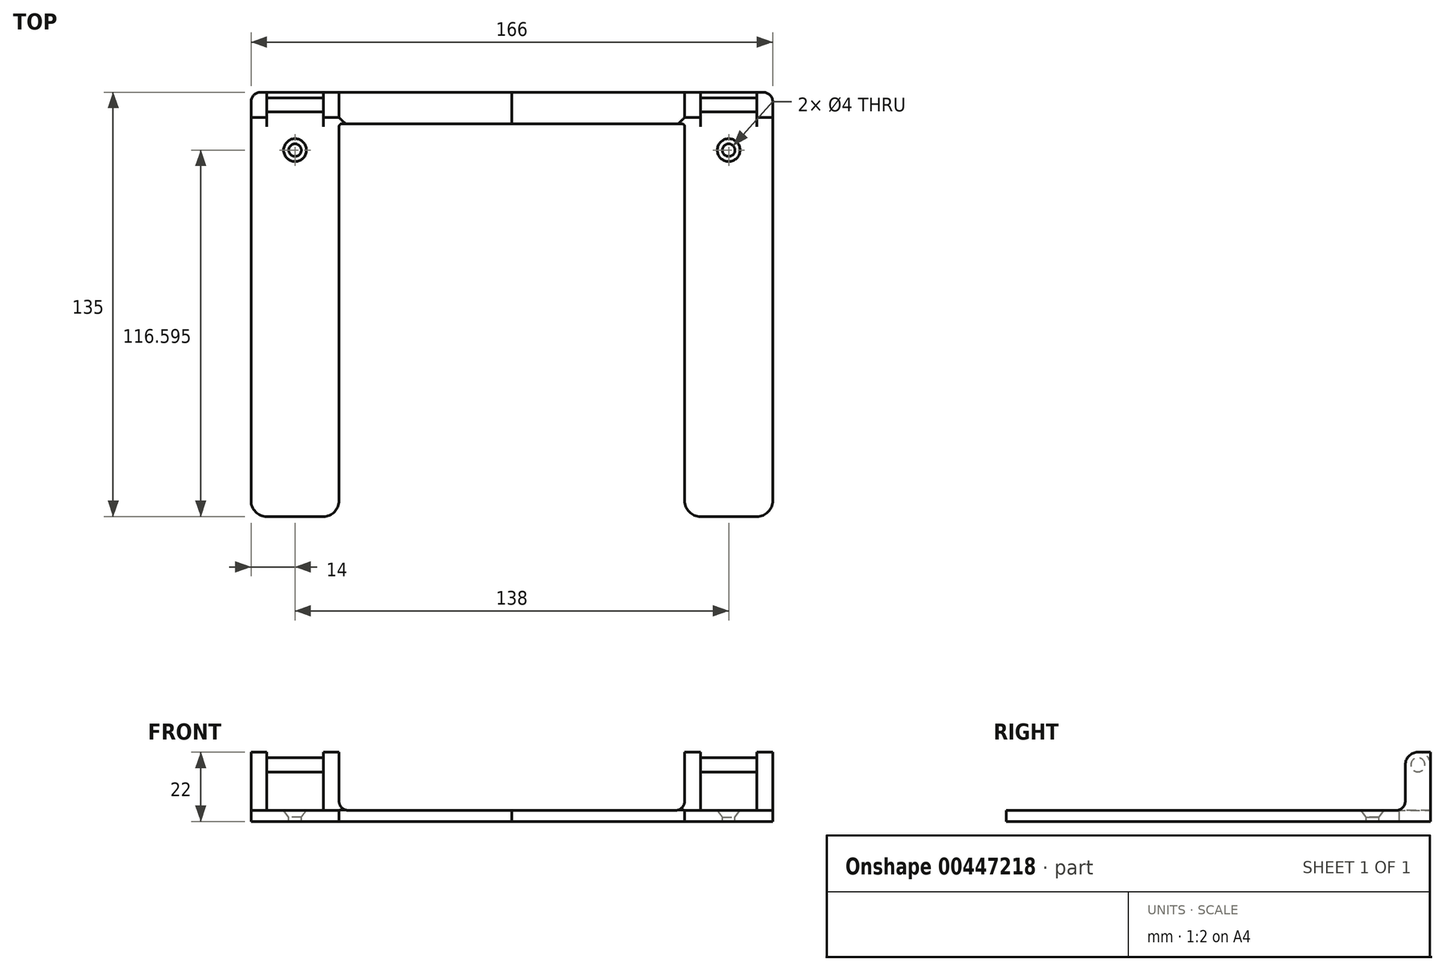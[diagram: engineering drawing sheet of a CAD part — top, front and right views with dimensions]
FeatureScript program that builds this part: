
annotation { "Feature Type Name" : "Feature", "Feature Type Description" : "" }
export const myFeature = defineFeature(function(context is Context, id is Id, definition is map)
    precondition{}
    {
        {
            var Q0;
            Q0=qCreatedBy(makeId("Top.planeOp"),FACE);
            var sketch = newSketch(context, id + "F0", { "sketchPlane" : qUnion([Q0])});
            skLineSegment(sketch, "E0.bottom", {"start": v(-83, 0) * mm, "end": v(-55, 0) * mm});
            skLineSegment(sketch, "E0.top", {"start": v(-83, 135) * mm, "end": v(0, 135) * mm});
            skLineSegment(sketch, "E0.left", {"start": v(-83, 0) * mm, "end": v(-83, 135) * mm});
            skLineSegment(sketch, "E1.top", {"start": v(-55, 125) * mm, "end": v(0, 125) * mm});
            skLineSegment(sketch, "E1.left", {"start": v(-55, 0) * mm, "end": v(-55, 125) * mm});
            skLineSegment(sketch, "E2", {"start": v(0, 135) * mm, "end": v(0, 125) * mm});
            skSolve(sketch);
        }
        {
            var Q0;
            Q0=qCreatedBy(makeId("Top.planeOp"),FACE);
            var sketch = newSketch(context, id + "F1", { "sketchPlane" : qUnion([Q0])});
            skLineSegment(sketch, "E3", {"start": v(-65.03, 100.86) * mm, "end": v(-64.7, 100.94) * mm});
            skLineSegment(sketch, "E4", {"start": v(-64.7, 100.94) * mm, "end": v(-62.94, 101.35) * mm});
            skLineSegment(sketch, "E5", {"start": v(-62.94, 101.35) * mm, "end": v(-61.22, 101.8) * mm});
            skLineSegment(sketch, "E6", {"start": v(-61.22, 101.8) * mm, "end": v(-60.9, 101.9) * mm});
            skLineSegment(sketch, "E7", {"start": v(-60.9, 101.9) * mm, "end": v(-60.65, 101.57) * mm});
            skLineSegment(sketch, "E8", {"start": v(-60.65, 101.57) * mm, "end": v(-60.06, 100.49) * mm});
            skLineSegment(sketch, "E9", {"start": v(-60.06, 100.49) * mm, "end": v(-59.39, 98.73) * mm});
            skLineSegment(sketch, "E10", {"start": v(-59.39, 98.73) * mm, "end": v(-58.9, 96.76) * mm});
            skLineSegment(sketch, "E11", {"start": v(-58.9, 96.76) * mm, "end": v(-58.67, 95.22) * mm});
            skLineSegment(sketch, "E12", {"start": v(-58.67, 95.22) * mm, "end": v(-58.64, 94.7) * mm});
            skLineSegment(sketch, "E13", {"start": v(-58.64, 94.7) * mm, "end": v(-58.62, 94.42) * mm});
            skLineSegment(sketch, "E14", {"start": v(-58.62, 94.42) * mm, "end": v(-58.62, 93.57) * mm});
            skLineSegment(sketch, "E15", {"start": v(-58.62, 93.57) * mm, "end": v(-58.71, 92.38) * mm});
            skLineSegment(sketch, "E16", {"start": v(-58.71, 92.38) * mm, "end": v(-58.94, 91.24) * mm});
            skLineSegment(sketch, "E17", {"start": v(-58.94, 91.24) * mm, "end": v(-59.32, 90.2) * mm});
            skLineSegment(sketch, "E18", {"start": v(-59.32, 90.2) * mm, "end": v(-59.87, 89.36) * mm});
            skLineSegment(sketch, "E19", {"start": v(-59.87, 89.36) * mm, "end": v(-60.6, 88.77) * mm});
            skLineSegment(sketch, "E20", {"start": v(-60.6, 88.77) * mm, "end": v(-61.53, 88.53) * mm});
            skLineSegment(sketch, "E21", {"start": v(-61.53, 88.53) * mm, "end": v(-62.4, 88.62) * mm});
            skLineSegment(sketch, "E22", {"start": v(-62.4, 88.62) * mm, "end": v(-62.67, 88.7) * mm});
            skLineSegment(sketch, "E23", {"start": v(-62.67, 88.7) * mm, "end": v(-63.05, 88.83) * mm});
            skLineSegment(sketch, "E24", {"start": v(-63.05, 88.83) * mm, "end": v(-64, 89.74) * mm});
            skLineSegment(sketch, "E25", {"start": v(-64, 89.74) * mm, "end": v(-65.04, 91.61) * mm});
            skLineSegment(sketch, "E26", {"start": v(-65.04, 91.61) * mm, "end": v(-65.65, 93.9) * mm});
            skLineSegment(sketch, "E27", {"start": v(-65.65, 93.9) * mm, "end": v(-65.79, 95.62) * mm});
            skLineSegment(sketch, "E28", {"start": v(-65.79, 95.62) * mm, "end": v(-65.72, 96.18) * mm});
            skLineSegment(sketch, "E29", {"start": v(-65.72, 96.18) * mm, "end": v(-65.69, 96.48) * mm});
            skLineSegment(sketch, "E30", {"start": v(-65.69, 96.48) * mm, "end": v(-65.51, 97.34) * mm});
            skLineSegment(sketch, "E31", {"start": v(-65.51, 97.34) * mm, "end": v(-65.24, 98.48) * mm});
            skLineSegment(sketch, "E32", {"start": v(-65.24, 98.48) * mm, "end": v(-65.03, 99.63) * mm});
            skLineSegment(sketch, "E33", {"start": v(-65.03, 99.63) * mm, "end": v(-65, 100.56) * mm});
            skLineSegment(sketch, "E34", {"start": v(-65, 100.56) * mm, "end": v(-65.03, 100.86) * mm});
            skLineSegment(sketch, "E35", {"start": v(-61.35, 103.49) * mm, "end": v(-61.66, 103.4) * mm});
            skLineSegment(sketch, "E36", {"start": v(-61.66, 103.4) * mm, "end": v(-63.42, 102.9) * mm});
            skLineSegment(sketch, "E37", {"start": v(-63.42, 102.9) * mm, "end": v(-65.16, 102.4) * mm});
            skLineSegment(sketch, "E38", {"start": v(-65.16, 102.4) * mm, "end": v(-65.46, 102.29) * mm});
            skLineSegment(sketch, "E39", {"start": v(-65.46, 102.29) * mm, "end": v(-65.6, 102.47) * mm});
            skLineSegment(sketch, "E40", {"start": v(-65.6, 102.47) * mm, "end": v(-65.92, 103.1) * mm});
            skLineSegment(sketch, "E41", {"start": v(-65.92, 103.1) * mm, "end": v(-66.24, 104.13) * mm});
            skLineSegment(sketch, "E42", {"start": v(-66.24, 104.13) * mm, "end": v(-66.38, 105.27) * mm});
            skLineSegment(sketch, "E43", {"start": v(-66.38, 105.27) * mm, "end": v(-66.32, 106.4) * mm});
            skLineSegment(sketch, "E44", {"start": v(-66.32, 106.4) * mm, "end": v(-66.03, 107.39) * mm});
            skLineSegment(sketch, "E45", {"start": v(-66.03, 107.39) * mm, "end": v(-65.5, 108.1) * mm});
            skLineSegment(sketch, "E46", {"start": v(-65.5, 108.1) * mm, "end": v(-64.69, 108.43) * mm});
            skLineSegment(sketch, "E47", {"start": v(-64.69, 108.43) * mm, "end": v(-63.83, 108.35) * mm});
            skLineSegment(sketch, "E48", {"start": v(-63.83, 108.35) * mm, "end": v(-63.57, 108.25) * mm});
            skLineSegment(sketch, "E49", {"start": v(-63.57, 108.25) * mm, "end": v(-63.3, 108.15) * mm});
            skLineSegment(sketch, "E50", {"start": v(-63.3, 108.15) * mm, "end": v(-62.62, 107.55) * mm});
            skLineSegment(sketch, "E51", {"start": v(-62.62, 107.55) * mm, "end": v(-61.96, 106.43) * mm});
            skLineSegment(sketch, "E52", {"start": v(-61.96, 106.43) * mm, "end": v(-61.55, 105.02) * mm});
            skLineSegment(sketch, "E53", {"start": v(-61.55, 105.02) * mm, "end": v(-61.38, 103.87) * mm});
            skLineSegment(sketch, "E54", {"start": v(-61.38, 103.87) * mm, "end": v(-61.35, 103.49) * mm});
            skLineSegment(sketch, "E55", {"start": v(-63.75, 67.11) * mm, "end": v(-63.4, 67.18) * mm});
            skLineSegment(sketch, "E56", {"start": v(-63.4, 67.18) * mm, "end": v(-61.65, 67.55) * mm});
            skLineSegment(sketch, "E57", {"start": v(-61.65, 67.55) * mm, "end": v(-59.91, 67.96) * mm});
            skLineSegment(sketch, "E58", {"start": v(-59.91, 67.96) * mm, "end": v(-59.6, 68.04) * mm});
            skLineSegment(sketch, "E59", {"start": v(-59.6, 68.04) * mm, "end": v(-59.35, 67.72) * mm});
            skLineSegment(sketch, "E60", {"start": v(-59.35, 67.72) * mm, "end": v(-58.79, 66.62) * mm});
            skLineSegment(sketch, "E61", {"start": v(-58.79, 66.62) * mm, "end": v(-58.15, 64.85) * mm});
            skLineSegment(sketch, "E62", {"start": v(-58.15, 64.85) * mm, "end": v(-57.71, 62.87) * mm});
            skLineSegment(sketch, "E63", {"start": v(-57.71, 62.87) * mm, "end": v(-57.52, 61.33) * mm});
            skLineSegment(sketch, "E64", {"start": v(-57.52, 61.33) * mm, "end": v(-57.5, 60.81) * mm});
            skLineSegment(sketch, "E65", {"start": v(-57.5, 60.81) * mm, "end": v(-57.48, 60.53) * mm});
            skLineSegment(sketch, "E66", {"start": v(-57.48, 60.53) * mm, "end": v(-57.5, 59.67) * mm});
            skLineSegment(sketch, "E67", {"start": v(-57.5, 59.67) * mm, "end": v(-57.63, 58.49) * mm});
            skLineSegment(sketch, "E68", {"start": v(-57.63, 58.49) * mm, "end": v(-57.88, 57.35) * mm});
            skLineSegment(sketch, "E69", {"start": v(-57.88, 57.35) * mm, "end": v(-58.29, 56.32) * mm});
            skLineSegment(sketch, "E70", {"start": v(-58.29, 56.32) * mm, "end": v(-58.85, 55.49) * mm});
            skLineSegment(sketch, "E71", {"start": v(-58.85, 55.49) * mm, "end": v(-59.6, 54.92) * mm});
            skLineSegment(sketch, "E72", {"start": v(-59.6, 54.92) * mm, "end": v(-60.53, 54.7) * mm});
            skLineSegment(sketch, "E73", {"start": v(-60.53, 54.7) * mm, "end": v(-61.4, 54.81) * mm});
            skLineSegment(sketch, "E74", {"start": v(-61.4, 54.81) * mm, "end": v(-61.67, 54.9) * mm});
            skLineSegment(sketch, "E75", {"start": v(-61.67, 54.9) * mm, "end": v(-62.04, 55.04) * mm});
            skLineSegment(sketch, "E76", {"start": v(-62.04, 55.04) * mm, "end": v(-62.98, 55.97) * mm});
            skLineSegment(sketch, "E77", {"start": v(-62.98, 55.97) * mm, "end": v(-63.97, 57.86) * mm});
            skLineSegment(sketch, "E78", {"start": v(-63.97, 57.86) * mm, "end": v(-64.53, 60.17) * mm});
            skLineSegment(sketch, "E79", {"start": v(-64.53, 60.17) * mm, "end": v(-64.62, 61.9) * mm});
            skLineSegment(sketch, "E80", {"start": v(-64.62, 61.9) * mm, "end": v(-64.54, 62.45) * mm});
            skLineSegment(sketch, "E81", {"start": v(-64.54, 62.45) * mm, "end": v(-64.5, 62.74) * mm});
            skLineSegment(sketch, "E82", {"start": v(-64.5, 62.74) * mm, "end": v(-64.3, 63.6) * mm});
            skLineSegment(sketch, "E83", {"start": v(-64.3, 63.6) * mm, "end": v(-64, 64.73) * mm});
            skLineSegment(sketch, "E84", {"start": v(-64, 64.73) * mm, "end": v(-63.77, 65.88) * mm});
            skLineSegment(sketch, "E85", {"start": v(-63.77, 65.88) * mm, "end": v(-63.72, 66.8) * mm});
            skLineSegment(sketch, "E86", {"start": v(-63.72, 66.8) * mm, "end": v(-63.75, 67.11) * mm});
            skLineSegment(sketch, "E87", {"start": v(-60, 69.65) * mm, "end": v(-60.32, 69.56) * mm});
            skLineSegment(sketch, "E88", {"start": v(-60.32, 69.56) * mm, "end": v(-62.08, 69.11) * mm});
            skLineSegment(sketch, "E89", {"start": v(-62.08, 69.11) * mm, "end": v(-63.83, 68.64) * mm});
            skLineSegment(sketch, "E90", {"start": v(-63.83, 68.64) * mm, "end": v(-64.14, 68.55) * mm});
            skLineSegment(sketch, "E91", {"start": v(-64.14, 68.55) * mm, "end": v(-64.28, 68.73) * mm});
            skLineSegment(sketch, "E92", {"start": v(-64.28, 68.73) * mm, "end": v(-64.59, 69.36) * mm});
            skLineSegment(sketch, "E93", {"start": v(-64.59, 69.36) * mm, "end": v(-64.88, 70.4) * mm});
            skLineSegment(sketch, "E94", {"start": v(-64.88, 70.4) * mm, "end": v(-65, 71.55) * mm});
            skLineSegment(sketch, "E95", {"start": v(-65, 71.55) * mm, "end": v(-64.9, 72.68) * mm});
            skLineSegment(sketch, "E96", {"start": v(-64.9, 72.68) * mm, "end": v(-64.6, 73.66) * mm});
            skLineSegment(sketch, "E97", {"start": v(-64.6, 73.66) * mm, "end": v(-64.04, 74.36) * mm});
            skLineSegment(sketch, "E98", {"start": v(-64.04, 74.36) * mm, "end": v(-63.22, 74.67) * mm});
            skLineSegment(sketch, "E99", {"start": v(-63.22, 74.67) * mm, "end": v(-62.37, 74.56) * mm});
            skLineSegment(sketch, "E100", {"start": v(-62.37, 74.56) * mm, "end": v(-62.12, 74.46) * mm});
            skLineSegment(sketch, "E101", {"start": v(-62.12, 74.46) * mm, "end": v(-61.86, 74.35) * mm});
            skLineSegment(sketch, "E102", {"start": v(-61.86, 74.35) * mm, "end": v(-61.18, 73.74) * mm});
            skLineSegment(sketch, "E103", {"start": v(-61.18, 73.74) * mm, "end": v(-60.54, 72.6) * mm});
            skLineSegment(sketch, "E104", {"start": v(-60.54, 72.6) * mm, "end": v(-60.17, 71.19) * mm});
            skLineSegment(sketch, "E105", {"start": v(-60.17, 71.19) * mm, "end": v(-60.02, 70.03) * mm});
            skLineSegment(sketch, "E106", {"start": v(-60.02, 70.03) * mm, "end": v(-60, 69.65) * mm});
            skLineSegment(sketch, "E107", {"start": v(-63.53, 33.44) * mm, "end": v(-63.18, 33.48) * mm});
            skLineSegment(sketch, "E108", {"start": v(-63.18, 33.48) * mm, "end": v(-61.4, 33.74) * mm});
            skLineSegment(sketch, "E109", {"start": v(-61.4, 33.74) * mm, "end": v(-59.64, 34.03) * mm});
            skLineSegment(sketch, "E110", {"start": v(-59.64, 34.03) * mm, "end": v(-59.32, 34.09) * mm});
            skLineSegment(sketch, "E111", {"start": v(-59.32, 34.09) * mm, "end": v(-59.1, 33.74) * mm});
            skLineSegment(sketch, "E112", {"start": v(-59.1, 33.74) * mm, "end": v(-58.62, 32.6) * mm});
            skLineSegment(sketch, "E113", {"start": v(-58.62, 32.6) * mm, "end": v(-58.1, 30.8) * mm});
            skLineSegment(sketch, "E114", {"start": v(-58.1, 30.8) * mm, "end": v(-57.8, 28.79) * mm});
            skLineSegment(sketch, "E115", {"start": v(-57.8, 28.79) * mm, "end": v(-57.72, 27.24) * mm});
            skLineSegment(sketch, "E116", {"start": v(-57.72, 27.24) * mm, "end": v(-57.73, 26.72) * mm});
            skLineSegment(sketch, "E117", {"start": v(-57.73, 26.72) * mm, "end": v(-57.74, 26.44) * mm});
            skLineSegment(sketch, "E118", {"start": v(-57.74, 26.44) * mm, "end": v(-57.82, 25.58) * mm});
            skLineSegment(sketch, "E119", {"start": v(-57.82, 25.58) * mm, "end": v(-58.02, 24.41) * mm});
            skLineSegment(sketch, "E120", {"start": v(-58.02, 24.41) * mm, "end": v(-58.36, 23.3) * mm});
            skLineSegment(sketch, "E121", {"start": v(-58.36, 23.3) * mm, "end": v(-58.83, 22.3) * mm});
            skLineSegment(sketch, "E122", {"start": v(-58.83, 22.3) * mm, "end": v(-59.45, 21.5) * mm});
            skLineSegment(sketch, "E123", {"start": v(-59.45, 21.5) * mm, "end": v(-60.23, 21) * mm});
            skLineSegment(sketch, "E124", {"start": v(-60.23, 21) * mm, "end": v(-61.18, 20.84) * mm});
            skLineSegment(sketch, "E125", {"start": v(-61.18, 20.84) * mm, "end": v(-62.04, 21.01) * mm});
            skLineSegment(sketch, "E126", {"start": v(-62.04, 21.01) * mm, "end": v(-62.3, 21.12) * mm});
            skLineSegment(sketch, "E127", {"start": v(-62.3, 21.12) * mm, "end": v(-62.67, 21.28) * mm});
            skLineSegment(sketch, "E128", {"start": v(-62.67, 21.28) * mm, "end": v(-63.54, 22.27) * mm});
            skLineSegment(sketch, "E129", {"start": v(-63.54, 22.27) * mm, "end": v(-64.4, 24.23) * mm});
            skLineSegment(sketch, "E130", {"start": v(-64.4, 24.23) * mm, "end": v(-64.8, 26.57) * mm});
            skLineSegment(sketch, "E131", {"start": v(-64.8, 26.57) * mm, "end": v(-64.76, 28.3) * mm});
            skLineSegment(sketch, "E132", {"start": v(-64.76, 28.3) * mm, "end": v(-64.65, 28.85) * mm});
            skLineSegment(sketch, "E133", {"start": v(-64.65, 28.85) * mm, "end": v(-64.59, 29.14) * mm});
            skLineSegment(sketch, "E134", {"start": v(-64.59, 29.14) * mm, "end": v(-64.33, 29.99) * mm});
            skLineSegment(sketch, "E135", {"start": v(-64.33, 29.99) * mm, "end": v(-63.95, 31.09) * mm});
            skLineSegment(sketch, "E136", {"start": v(-63.95, 31.09) * mm, "end": v(-63.64, 32.22) * mm});
            skLineSegment(sketch, "E137", {"start": v(-63.64, 32.22) * mm, "end": v(-63.52, 33.14) * mm});
            skLineSegment(sketch, "E138", {"start": v(-63.52, 33.14) * mm, "end": v(-63.53, 33.44) * mm});
            skLineSegment(sketch, "E139", {"start": v(-59.62, 35.71) * mm, "end": v(-59.93, 35.65) * mm});
            skLineSegment(sketch, "E140", {"start": v(-59.93, 35.65) * mm, "end": v(-61.73, 35.32) * mm});
            skLineSegment(sketch, "E141", {"start": v(-61.73, 35.32) * mm, "end": v(-63.5, 34.98) * mm});
            skLineSegment(sketch, "E142", {"start": v(-63.5, 34.98) * mm, "end": v(-63.82, 34.9) * mm});
            skLineSegment(sketch, "E143", {"start": v(-63.82, 34.9) * mm, "end": v(-63.95, 35.1) * mm});
            skLineSegment(sketch, "E144", {"start": v(-63.95, 35.1) * mm, "end": v(-64.2, 35.75) * mm});
            skLineSegment(sketch, "E145", {"start": v(-64.2, 35.75) * mm, "end": v(-64.43, 36.8) * mm});
            skLineSegment(sketch, "E146", {"start": v(-64.43, 36.8) * mm, "end": v(-64.46, 37.96) * mm});
            skLineSegment(sketch, "E147", {"start": v(-64.46, 37.96) * mm, "end": v(-64.3, 39.08) * mm});
            skLineSegment(sketch, "E148", {"start": v(-64.3, 39.08) * mm, "end": v(-63.92, 40.03) * mm});
            skLineSegment(sketch, "E149", {"start": v(-63.92, 40.03) * mm, "end": v(-63.31, 40.7) * mm});
            skLineSegment(sketch, "E150", {"start": v(-63.31, 40.7) * mm, "end": v(-62.48, 40.95) * mm});
            skLineSegment(sketch, "E151", {"start": v(-62.48, 40.95) * mm, "end": v(-61.64, 40.78) * mm});
            skLineSegment(sketch, "E152", {"start": v(-61.64, 40.78) * mm, "end": v(-61.39, 40.66) * mm});
            skLineSegment(sketch, "E153", {"start": v(-61.39, 40.66) * mm, "end": v(-61.13, 40.53) * mm});
            skLineSegment(sketch, "E154", {"start": v(-61.13, 40.53) * mm, "end": v(-60.5, 39.88) * mm});
            skLineSegment(sketch, "E155", {"start": v(-60.5, 39.88) * mm, "end": v(-59.95, 38.7) * mm});
            skLineSegment(sketch, "E156", {"start": v(-59.95, 38.7) * mm, "end": v(-59.67, 37.26) * mm});
            skLineSegment(sketch, "E157", {"start": v(-59.67, 37.26) * mm, "end": v(-59.6, 36.1) * mm});
            skLineSegment(sketch, "E158", {"start": v(-59.6, 36.1) * mm, "end": v(-59.62, 35.71) * mm});
            skLineSegment(sketch, "E159", {"start": v(-73.59, 84.3) * mm, "end": v(-73.93, 84.31) * mm});
            skLineSegment(sketch, "E160", {"start": v(-73.93, 84.31) * mm, "end": v(-75.73, 84.38) * mm});
            skLineSegment(sketch, "E161", {"start": v(-75.73, 84.38) * mm, "end": v(-77.5, 84.5) * mm});
            skLineSegment(sketch, "E162", {"start": v(-77.5, 84.5) * mm, "end": v(-77.84, 84.52) * mm});
            skLineSegment(sketch, "E163", {"start": v(-77.84, 84.52) * mm, "end": v(-78.06, 84.07) * mm});
            skLineSegment(sketch, "E164", {"start": v(-78.06, 84.07) * mm, "end": v(-78.72, 81.12) * mm});
            skLineSegment(sketch, "E165", {"start": v(-78.72, 81.12) * mm, "end": v(-78.76, 77.7) * mm});
            skLineSegment(sketch, "E166", {"start": v(-78.76, 77.7) * mm, "end": v(-78.67, 77.03) * mm});
            skLineSegment(sketch, "E167", {"start": v(-78.67, 77.03) * mm, "end": v(-78.64, 76.75) * mm});
            skLineSegment(sketch, "E168", {"start": v(-78.64, 76.75) * mm, "end": v(-78.47, 75.9) * mm});
            skLineSegment(sketch, "E169", {"start": v(-78.47, 75.9) * mm, "end": v(-78.15, 74.76) * mm});
            skLineSegment(sketch, "E170", {"start": v(-78.15, 74.76) * mm, "end": v(-77.7, 73.68) * mm});
            skLineSegment(sketch, "E171", {"start": v(-77.7, 73.68) * mm, "end": v(-77.13, 72.74) * mm});
            skLineSegment(sketch, "E172", {"start": v(-77.13, 72.74) * mm, "end": v(-76.43, 72.02) * mm});
            skLineSegment(sketch, "E173", {"start": v(-76.43, 72.02) * mm, "end": v(-75.6, 71.59) * mm});
            skLineSegment(sketch, "E174", {"start": v(-75.6, 71.59) * mm, "end": v(-74.65, 71.53) * mm});
            skLineSegment(sketch, "E175", {"start": v(-74.65, 71.53) * mm, "end": v(-73.8, 71.78) * mm});
            skLineSegment(sketch, "E176", {"start": v(-73.8, 71.78) * mm, "end": v(-73.56, 71.92) * mm});
            skLineSegment(sketch, "E177", {"start": v(-73.56, 71.92) * mm, "end": v(-73.21, 72.12) * mm});
            skLineSegment(sketch, "E178", {"start": v(-73.21, 72.12) * mm, "end": v(-72.45, 73.2) * mm});
            skLineSegment(sketch, "E179", {"start": v(-72.45, 73.2) * mm, "end": v(-71.8, 75.23) * mm});
            skLineSegment(sketch, "E180", {"start": v(-71.8, 75.23) * mm, "end": v(-71.63, 77.6) * mm});
            skLineSegment(sketch, "E181", {"start": v(-71.63, 77.6) * mm, "end": v(-71.84, 79.31) * mm});
            skLineSegment(sketch, "E182", {"start": v(-71.84, 79.31) * mm, "end": v(-72, 79.85) * mm});
            skLineSegment(sketch, "E183", {"start": v(-72, 79.85) * mm, "end": v(-72.1, 80.13) * mm});
            skLineSegment(sketch, "E184", {"start": v(-72.1, 80.13) * mm, "end": v(-72.44, 80.95) * mm});
            skLineSegment(sketch, "E185", {"start": v(-72.44, 80.95) * mm, "end": v(-72.93, 82) * mm});
            skLineSegment(sketch, "E186", {"start": v(-72.93, 82) * mm, "end": v(-73.35, 83.1) * mm});
            skLineSegment(sketch, "E187", {"start": v(-73.35, 83.1) * mm, "end": v(-73.56, 84) * mm});
            skLineSegment(sketch, "E188", {"start": v(-73.56, 84) * mm, "end": v(-73.59, 84.3) * mm});
            skLineSegment(sketch, "E189", {"start": v(-77.7, 86.17) * mm, "end": v(-77.39, 86.13) * mm});
            skLineSegment(sketch, "E190", {"start": v(-77.39, 86.13) * mm, "end": v(-75.57, 86) * mm});
            skLineSegment(sketch, "E191", {"start": v(-75.57, 86) * mm, "end": v(-73.76, 85.83) * mm});
            skLineSegment(sketch, "E192", {"start": v(-73.76, 85.83) * mm, "end": v(-73.45, 85.79) * mm});
            skLineSegment(sketch, "E193", {"start": v(-73.45, 85.79) * mm, "end": v(-73.34, 85.99) * mm});
            skLineSegment(sketch, "E194", {"start": v(-73.34, 85.99) * mm, "end": v(-73.14, 86.66) * mm});
            skLineSegment(sketch, "E195", {"start": v(-73.14, 86.66) * mm, "end": v(-73.04, 87.74) * mm});
            skLineSegment(sketch, "E196", {"start": v(-73.04, 87.74) * mm, "end": v(-73.12, 88.9) * mm});
            skLineSegment(sketch, "E197", {"start": v(-73.12, 88.9) * mm, "end": v(-73.4, 89.99) * mm});
            skLineSegment(sketch, "E198", {"start": v(-73.4, 89.99) * mm, "end": v(-73.87, 90.9) * mm});
            skLineSegment(sketch, "E199", {"start": v(-73.87, 90.9) * mm, "end": v(-74.53, 91.5) * mm});
            skLineSegment(sketch, "E200", {"start": v(-74.53, 91.5) * mm, "end": v(-75.4, 91.67) * mm});
            skLineSegment(sketch, "E201", {"start": v(-75.4, 91.67) * mm, "end": v(-76.2, 91.42) * mm});
            skLineSegment(sketch, "E202", {"start": v(-76.2, 91.42) * mm, "end": v(-76.44, 91.27) * mm});
            skLineSegment(sketch, "E203", {"start": v(-76.44, 91.27) * mm, "end": v(-76.68, 91.12) * mm});
            skLineSegment(sketch, "E204", {"start": v(-76.68, 91.12) * mm, "end": v(-77.25, 90.4) * mm});
            skLineSegment(sketch, "E205", {"start": v(-77.25, 90.4) * mm, "end": v(-77.68, 89.17) * mm});
            skLineSegment(sketch, "E206", {"start": v(-77.68, 89.17) * mm, "end": v(-77.81, 87.71) * mm});
            skLineSegment(sketch, "E207", {"start": v(-77.81, 87.71) * mm, "end": v(-77.75, 86.55) * mm});
            skLineSegment(sketch, "E208", {"start": v(-77.75, 86.55) * mm, "end": v(-77.7, 86.17) * mm});
            skLineSegment(sketch, "E209", {"start": v(-73.59, 50.5) * mm, "end": v(-73.93, 50.52) * mm});
            skLineSegment(sketch, "E210", {"start": v(-73.93, 50.52) * mm, "end": v(-75.73, 50.59) * mm});
            skLineSegment(sketch, "E211", {"start": v(-75.73, 50.59) * mm, "end": v(-77.5, 50.7) * mm});
            skLineSegment(sketch, "E212", {"start": v(-77.5, 50.7) * mm, "end": v(-77.84, 50.72) * mm});
            skLineSegment(sketch, "E213", {"start": v(-77.84, 50.72) * mm, "end": v(-78.06, 50.27) * mm});
            skLineSegment(sketch, "E214", {"start": v(-78.06, 50.27) * mm, "end": v(-78.72, 47.33) * mm});
            skLineSegment(sketch, "E215", {"start": v(-78.72, 47.33) * mm, "end": v(-78.76, 43.91) * mm});
            skLineSegment(sketch, "E216", {"start": v(-78.76, 43.91) * mm, "end": v(-78.67, 43.24) * mm});
            skLineSegment(sketch, "E217", {"start": v(-78.67, 43.24) * mm, "end": v(-78.64, 42.95) * mm});
            skLineSegment(sketch, "E218", {"start": v(-78.64, 42.95) * mm, "end": v(-78.47, 42.1) * mm});
            skLineSegment(sketch, "E219", {"start": v(-78.47, 42.1) * mm, "end": v(-78.15, 40.97) * mm});
            skLineSegment(sketch, "E220", {"start": v(-78.15, 40.97) * mm, "end": v(-77.7, 39.89) * mm});
            skLineSegment(sketch, "E221", {"start": v(-77.7, 39.89) * mm, "end": v(-77.13, 38.94) * mm});
            skLineSegment(sketch, "E222", {"start": v(-77.13, 38.94) * mm, "end": v(-76.43, 38.22) * mm});
            skLineSegment(sketch, "E223", {"start": v(-76.43, 38.22) * mm, "end": v(-75.6, 37.8) * mm});
            skLineSegment(sketch, "E224", {"start": v(-75.6, 37.8) * mm, "end": v(-74.65, 37.73) * mm});
            skLineSegment(sketch, "E225", {"start": v(-74.65, 37.73) * mm, "end": v(-73.8, 37.99) * mm});
            skLineSegment(sketch, "E226", {"start": v(-73.8, 37.99) * mm, "end": v(-73.56, 38.13) * mm});
            skLineSegment(sketch, "E227", {"start": v(-73.56, 38.13) * mm, "end": v(-73.21, 38.32) * mm});
            skLineSegment(sketch, "E228", {"start": v(-73.21, 38.32) * mm, "end": v(-72.45, 39.4) * mm});
            skLineSegment(sketch, "E229", {"start": v(-72.45, 39.4) * mm, "end": v(-71.8, 41.43) * mm});
            skLineSegment(sketch, "E230", {"start": v(-71.8, 41.43) * mm, "end": v(-71.63, 43.8) * mm});
            skLineSegment(sketch, "E231", {"start": v(-71.63, 43.8) * mm, "end": v(-71.84, 45.51) * mm});
            skLineSegment(sketch, "E232", {"start": v(-71.84, 45.51) * mm, "end": v(-72, 46.05) * mm});
            skLineSegment(sketch, "E233", {"start": v(-72, 46.05) * mm, "end": v(-72.1, 46.33) * mm});
            skLineSegment(sketch, "E234", {"start": v(-72.1, 46.33) * mm, "end": v(-72.44, 47.15) * mm});
            skLineSegment(sketch, "E235", {"start": v(-72.44, 47.15) * mm, "end": v(-72.93, 48.2) * mm});
            skLineSegment(sketch, "E236", {"start": v(-72.93, 48.2) * mm, "end": v(-73.35, 49.3) * mm});
            skLineSegment(sketch, "E237", {"start": v(-73.35, 49.3) * mm, "end": v(-73.56, 50.2) * mm});
            skLineSegment(sketch, "E238", {"start": v(-73.56, 50.2) * mm, "end": v(-73.59, 50.5) * mm});
            skLineSegment(sketch, "E239", {"start": v(-77.7, 52.37) * mm, "end": v(-77.39, 52.34) * mm});
            skLineSegment(sketch, "E240", {"start": v(-77.39, 52.34) * mm, "end": v(-75.57, 52.2) * mm});
            skLineSegment(sketch, "E241", {"start": v(-75.57, 52.2) * mm, "end": v(-73.76, 52.03) * mm});
            skLineSegment(sketch, "E242", {"start": v(-73.76, 52.03) * mm, "end": v(-73.45, 51.99) * mm});
            skLineSegment(sketch, "E243", {"start": v(-73.45, 51.99) * mm, "end": v(-73.34, 52.2) * mm});
            skLineSegment(sketch, "E244", {"start": v(-73.34, 52.2) * mm, "end": v(-73.14, 52.87) * mm});
            skLineSegment(sketch, "E245", {"start": v(-73.14, 52.87) * mm, "end": v(-73.04, 53.95) * mm});
            skLineSegment(sketch, "E246", {"start": v(-73.04, 53.95) * mm, "end": v(-73.12, 55.1) * mm});
            skLineSegment(sketch, "E247", {"start": v(-73.12, 55.1) * mm, "end": v(-73.4, 56.19) * mm});
            skLineSegment(sketch, "E248", {"start": v(-73.4, 56.19) * mm, "end": v(-73.87, 57.1) * mm});
            skLineSegment(sketch, "E249", {"start": v(-73.87, 57.1) * mm, "end": v(-74.53, 57.7) * mm});
            skLineSegment(sketch, "E250", {"start": v(-74.53, 57.7) * mm, "end": v(-75.4, 57.87) * mm});
            skLineSegment(sketch, "E251", {"start": v(-75.4, 57.87) * mm, "end": v(-76.2, 57.62) * mm});
            skLineSegment(sketch, "E252", {"start": v(-76.2, 57.62) * mm, "end": v(-76.44, 57.47) * mm});
            skLineSegment(sketch, "E253", {"start": v(-76.44, 57.47) * mm, "end": v(-76.68, 57.32) * mm});
            skLineSegment(sketch, "E254", {"start": v(-76.68, 57.32) * mm, "end": v(-77.25, 56.6) * mm});
            skLineSegment(sketch, "E255", {"start": v(-77.25, 56.6) * mm, "end": v(-77.68, 55.37) * mm});
            skLineSegment(sketch, "E256", {"start": v(-77.68, 55.37) * mm, "end": v(-77.81, 53.92) * mm});
            skLineSegment(sketch, "E257", {"start": v(-77.81, 53.92) * mm, "end": v(-77.75, 52.75) * mm});
            skLineSegment(sketch, "E258", {"start": v(-77.75, 52.75) * mm, "end": v(-77.7, 52.37) * mm});
            skLineSegment(sketch, "E259", {"start": v(-72.58, 16.71) * mm, "end": v(-72.93, 16.72) * mm});
            skLineSegment(sketch, "E260", {"start": v(-72.93, 16.72) * mm, "end": v(-74.73, 16.8) * mm});
            skLineSegment(sketch, "E261", {"start": v(-74.73, 16.8) * mm, "end": v(-76.5, 16.9) * mm});
            skLineSegment(sketch, "E262", {"start": v(-76.5, 16.9) * mm, "end": v(-76.84, 16.92) * mm});
            skLineSegment(sketch, "E263", {"start": v(-76.84, 16.92) * mm, "end": v(-77.06, 16.48) * mm});
            skLineSegment(sketch, "E264", {"start": v(-77.06, 16.48) * mm, "end": v(-77.71, 13.53) * mm});
            skLineSegment(sketch, "E265", {"start": v(-77.71, 13.53) * mm, "end": v(-77.76, 10.12) * mm});
            skLineSegment(sketch, "E266", {"start": v(-77.76, 10.12) * mm, "end": v(-77.67, 9.44) * mm});
            skLineSegment(sketch, "E267", {"start": v(-77.67, 9.44) * mm, "end": v(-77.63, 9.16) * mm});
            skLineSegment(sketch, "E268", {"start": v(-77.63, 9.16) * mm, "end": v(-77.47, 8.31) * mm});
            skLineSegment(sketch, "E269", {"start": v(-77.47, 8.31) * mm, "end": v(-77.15, 7.17) * mm});
            skLineSegment(sketch, "E270", {"start": v(-77.15, 7.17) * mm, "end": v(-76.7, 6.09) * mm});
            skLineSegment(sketch, "E271", {"start": v(-76.7, 6.09) * mm, "end": v(-76.13, 5.15) * mm});
            skLineSegment(sketch, "E272", {"start": v(-76.13, 5.15) * mm, "end": v(-75.43, 4.42) * mm});
            skLineSegment(sketch, "E273", {"start": v(-75.43, 4.42) * mm, "end": v(-74.6, 4) * mm});
            skLineSegment(sketch, "E274", {"start": v(-74.6, 4) * mm, "end": v(-73.64, 3.94) * mm});
            skLineSegment(sketch, "E275", {"start": v(-73.64, 3.94) * mm, "end": v(-72.8, 4.2) * mm});
            skLineSegment(sketch, "E276", {"start": v(-72.8, 4.2) * mm, "end": v(-72.55, 4.33) * mm});
            skLineSegment(sketch, "E277", {"start": v(-72.55, 4.33) * mm, "end": v(-72.2, 4.52) * mm});
            skLineSegment(sketch, "E278", {"start": v(-72.2, 4.52) * mm, "end": v(-71.44, 5.6) * mm});
            skLineSegment(sketch, "E279", {"start": v(-71.44, 5.6) * mm, "end": v(-70.79, 7.64) * mm});
            skLineSegment(sketch, "E280", {"start": v(-70.79, 7.64) * mm, "end": v(-70.63, 10) * mm});
            skLineSegment(sketch, "E281", {"start": v(-70.63, 10) * mm, "end": v(-70.83, 11.72) * mm});
            skLineSegment(sketch, "E282", {"start": v(-70.83, 11.72) * mm, "end": v(-71, 12.26) * mm});
            skLineSegment(sketch, "E283", {"start": v(-71, 12.26) * mm, "end": v(-71.1, 12.54) * mm});
            skLineSegment(sketch, "E284", {"start": v(-71.1, 12.54) * mm, "end": v(-71.44, 13.35) * mm});
            skLineSegment(sketch, "E285", {"start": v(-71.44, 13.35) * mm, "end": v(-71.92, 14.4) * mm});
            skLineSegment(sketch, "E286", {"start": v(-71.92, 14.4) * mm, "end": v(-72.35, 15.5) * mm});
            skLineSegment(sketch, "E287", {"start": v(-72.35, 15.5) * mm, "end": v(-72.56, 16.4) * mm});
            skLineSegment(sketch, "E288", {"start": v(-72.56, 16.4) * mm, "end": v(-72.58, 16.71) * mm});
            skLineSegment(sketch, "E289", {"start": v(-76.7, 18.58) * mm, "end": v(-76.38, 18.54) * mm});
            skLineSegment(sketch, "E290", {"start": v(-76.38, 18.54) * mm, "end": v(-74.56, 18.4) * mm});
            skLineSegment(sketch, "E291", {"start": v(-74.56, 18.4) * mm, "end": v(-72.76, 18.24) * mm});
            skLineSegment(sketch, "E292", {"start": v(-72.76, 18.24) * mm, "end": v(-72.44, 18.2) * mm});
            skLineSegment(sketch, "E293", {"start": v(-72.44, 18.2) * mm, "end": v(-72.33, 18.4) * mm});
            skLineSegment(sketch, "E294", {"start": v(-72.33, 18.4) * mm, "end": v(-72.14, 19.07) * mm});
            skLineSegment(sketch, "E295", {"start": v(-72.14, 19.07) * mm, "end": v(-72.03, 20.15) * mm});
            skLineSegment(sketch, "E296", {"start": v(-72.03, 20.15) * mm, "end": v(-72.12, 21.3) * mm});
            skLineSegment(sketch, "E297", {"start": v(-72.12, 21.3) * mm, "end": v(-72.4, 22.4) * mm});
            skLineSegment(sketch, "E298", {"start": v(-72.4, 22.4) * mm, "end": v(-72.86, 23.3) * mm});
            skLineSegment(sketch, "E299", {"start": v(-72.86, 23.3) * mm, "end": v(-73.53, 23.9) * mm});
            skLineSegment(sketch, "E300", {"start": v(-73.53, 23.9) * mm, "end": v(-74.39, 24.07) * mm});
            skLineSegment(sketch, "E301", {"start": v(-74.39, 24.07) * mm, "end": v(-75.2, 23.82) * mm});
            skLineSegment(sketch, "E302", {"start": v(-75.2, 23.82) * mm, "end": v(-75.44, 23.68) * mm});
            skLineSegment(sketch, "E303", {"start": v(-75.44, 23.68) * mm, "end": v(-75.68, 23.53) * mm});
            skLineSegment(sketch, "E304", {"start": v(-75.68, 23.53) * mm, "end": v(-76.25, 22.8) * mm});
            skLineSegment(sketch, "E305", {"start": v(-76.25, 22.8) * mm, "end": v(-76.68, 21.58) * mm});
            skLineSegment(sketch, "E306", {"start": v(-76.68, 21.58) * mm, "end": v(-76.8, 20.12) * mm});
            skLineSegment(sketch, "E307", {"start": v(-76.8, 20.12) * mm, "end": v(-76.75, 18.96) * mm});
            skLineSegment(sketch, "E308", {"start": v(-76.75, 18.96) * mm, "end": v(-76.7, 18.58) * mm});
            skSolve(sketch);
        }
        {
            var Q0;
            {var subQ6=sQuery(id+"F0.wireOp",EDGE,"E0.top");Q0=makeQuery(id+"F0.imprint","IMPRINT",FACE,{"disambiguationData":[TD([[makeQuery(id+"F0.imprint","IMPRINT",EDGE,{"derivedFrom":subQ6}),-1.0]])]});}
            extrude(context, id + "F2", {"entities" : qUnion([Q0]), "depth" : 3.5 * mm, "offsetDistance" : 25 * mm});
        }
        {
            var Q0;
            {var subQ8=sQuery(id+"F0.wireOp",EDGE,"u4QvhtKX-iDNZ-ps5d-BxI4-3EPHAVPvSog8");Q0=makeQuery(id+"F0.imprint","IMPRINT",FACE,{"disambiguationData":[TD([[makeQuery(id+"F0.imprint","IMPRINT",EDGE,{"derivedFrom":subQ8}),1.0]])]});}
            var Q1;
            {var subQ5=sQuery(id+"F0.wireOp",EDGE,"79211e8e-8244-4d67-8351-19a3457fbf290.MirrorCS");Q1=makeQuery(id+"F0.imprint","IMPRINT",FACE,{"disambiguationData":[TD([[makeQuery(id+"F0.imprint","IMPRINT",EDGE,{"derivedFrom":subQ5}),-1.0]])]});}
            var Q2;
            {var subQ0=sQuery(id+"F0.wireOp",EDGE,"E0.right");var subQ1=sQuery(id+"F0.wireOp",EDGE,"E0.bottom");var subQ2=makeQuery(id+"F0.imprint","INTERSECT",VERTEX,{"derivedFrom":[subQ1,subQ0]});Q2=makeQuery(id+"F0.imprint","IMPRINT",FACE,{"disambiguationData":[TD([[makeQuery(id+"F0.imprint","IMPRINT",EDGE,{"disambiguationData":[TD([[subQ2,-1.0]])],"derivedFrom":subQ0}),1.0]])]});}
            var Q3;
            {var subQ1=sQuery(id+"F0.wireOp",EDGE,"E1.bottom");var subQ3=sQuery(id+"F0.wireOp",EDGE,"5d9b1bdb-1e1e-4ad1-b13f-3cf6168354ab0.MirrorCS");var subQ4=makeQuery(id+"F0.imprint","INTERSECT",VERTEX,{"derivedFrom":[subQ1,subQ3]});Q3=makeQuery(id+"F0.imprint","IMPRINT",FACE,{"disambiguationData":[TD([[makeQuery(id+"F0.imprint","IMPRINT",EDGE,{"disambiguationData":[TD([[subQ4,1.0]])],"derivedFrom":subQ3}),1.0]])]});}
            var Q4;
            {var subQ0=sQuery(id+"F0.wireOp",EDGE,"E0.left");var subQ1=sQuery(id+"F0.wireOp",EDGE,"E0.bottom");var subQ2=makeQuery(id+"F0.imprint","INTERSECT",VERTEX,{"derivedFrom":[subQ1,subQ0]});Q4=makeQuery(id+"F0.imprint","IMPRINT",FACE,{"disambiguationData":[TD([[makeQuery(id+"F0.imprint","IMPRINT",EDGE,{"disambiguationData":[TD([[subQ2,-1.0]])],"derivedFrom":subQ0}),-1.0]])]});}
            var Q5;
            {var subQ1=sQuery(id+"F0.wireOp",EDGE,"E1.bottom");var subQ3=sQuery(id+"F0.wireOp",EDGE,"aedadd35-a89c-44a4-b081-527595949099");var subQ4=makeQuery(id+"F0.imprint","INTERSECT",VERTEX,{"derivedFrom":[subQ1,subQ3]});Q5=makeQuery(id+"F0.imprint","IMPRINT",FACE,{"disambiguationData":[TD([[makeQuery(id+"F0.imprint","IMPRINT",EDGE,{"disambiguationData":[TD([[subQ4,1.0]])],"derivedFrom":subQ3}),-1.0]])]});}
            extrude(context, id + "F3", {"entities" : qUnion([Q0, Q1, Q2, Q3, Q4, Q5]), "operationType" : NewBodyOperationType.ADD, "depth" : 2 * mm, "offsetDistance" : 25 * mm});
        }
        {
            var Q0;
            Q0=qCreatedBy(makeId("Right.planeOp"),FACE);
            var Q1;
            Q1=sQuery(id+"F0.wireOp",VERTEX,"E0.left.end");
            cPlane(context, id + "F4", {"entities" : qUnion([Q0, Q1]), "cplaneType" : CPlaneType.PLANE_POINT, "offset" : 25 * mm, "width" : 150 * mm, "height" : 150 * mm});
        }
        {
            var Q0;
            Q0=qCreatedBy(id+"F4.planeOp",FACE);
            var sketch = newSketch(context, id + "F5", { "sketchPlane" : qUnion([Q0])});
            skCircle(sketch, "E309", {"center": v(131, 18) * mm, "radius": 2.25 * mm});
            skLineSegment(sketch, "E310.bottom", {"start": v(127, 22) * mm, "end": v(135, 22) * mm});
            skLineSegment(sketch, "E310.top", {"start": v(127, 0) * mm, "end": v(135, 0) * mm});
            skLineSegment(sketch, "E310.left", {"start": v(127, 22) * mm, "end": v(127, 0) * mm});
            skLineSegment(sketch, "E310.right", {"start": v(135, 22) * mm, "end": v(135, 0) * mm});
            skSolve(sketch);
        }
        {
            var Q0;
            Q0=qCreatedBy(id+"F4.planeOp",FACE);
            cPlane(context, id + "F6", {"entities" : qUnion([Q0]), "cplaneType" : CPlaneType.OFFSET, "offset" : 28 * mm, "width" : 150 * mm, "height" : 150 * mm});
        }
        {
            var Q0;
            Q0=makeQuery(id+"F5.imprint","IMPRINT",FACE,{"disambiguationData":[TD([[makeQuery(id+"F5.imprint","IMPRINT",EDGE,{"derivedFrom":sQuery(id+"F5.wireOp",EDGE,"E309")}),-1.0]])]});
            var Q1;
            Q1=makeQuery(id+"F5.imprint","IMPRINT",FACE,{"disambiguationData":[TD([[makeQuery(id+"F5.imprint","IMPRINT",EDGE,{"derivedFrom":sQuery(id+"F5.wireOp",EDGE,"E309")}),1.0]])]});
            extrude(context, id + "F7", {"entities" : qUnion([Q0, Q1]), "operationType" : NewBodyOperationType.ADD, "depth" : 5 * mm, "offsetDistance" : 25 * mm});
        }
        {
            var Q0;
            Q0=qCreatedBy(id+"F6.planeOp",FACE);
            var sketch = newSketch(context, id + "F8", { "sketchPlane" : qUnion([Q0])});
            skLineSegment(sketch, "E311.bottom", {"start": v(135, 0) * mm, "end": v(127, 0) * mm});
            skLineSegment(sketch, "E311.top", {"start": v(135, 22) * mm, "end": v(127, 22) * mm});
            skLineSegment(sketch, "E311.left", {"start": v(135, 0) * mm, "end": v(135, 22) * mm});
            skLineSegment(sketch, "E311.right", {"start": v(127, 0) * mm, "end": v(127, 22) * mm});
            skSolve(sketch);
        }
        {
            var Q0;
            Q0=makeQuery(id+"F8.imprint","IMPRINT",FACE,{"disambiguationData":[TD([[makeQuery(id+"F8.imprint","IMPRINT",EDGE,{"derivedFrom":sQuery(id+"F8.wireOp",EDGE,"E311.bottom")}),-1.0]])]});
            extrude(context, id + "F9", {"entities" : qUnion([Q0]), "operationType" : NewBodyOperationType.ADD, "oppositeDirection" : true, "depth" : 5 * mm, "offsetDistance" : 25 * mm});
        }
        {
            var Q0;
            Q0=makeQuery(id+"F5.imprint","IMPRINT",FACE,{"disambiguationData":[TD([[makeQuery(id+"F5.imprint","IMPRINT",EDGE,{"derivedFrom":sQuery(id+"F5.wireOp",EDGE,"E309")}),1.0]])]});
            var Q1;
            Q1=makeQuery(id+"F9.opExtrude","CAP_FACE",FACE,{"disambiguationData":[OSD([sQuery(id+"F8.wireOp",EDGE,"E311.bottom"),sQuery(id+"F8.wireOp",EDGE,"E311.top"),sQuery(id+"F8.wireOp",EDGE,"E311.left"),sQuery(id+"F8.wireOp",EDGE,"E311.right")])],"isStart":false});
            extrude(context, id + "F10", {"entities" : qUnion([Q0]), "operationType" : NewBodyOperationType.ADD, "endBound" : BoundingType.UP_TO_SURFACE, "depth" : 32 * mm, "endBoundEntityFace" : qUnion([Q1]), "offsetDistance" : 25 * mm});
        }
        {
            var Q0;
            Q0=makeQuery(id+"F2.opExtrude","SWEPT_EDGE",EDGE,{"disambiguationData":[OSD([sQuery(id+"F0.wireOp",EDGE,"E0.top"),sQuery(id+"F0.wireOp",EDGE,"E0.left")])]});
            fillet(context, id + "F11", {"entities" : qUnion([Q0]), "radius" : 3 * mm, "tangentPropagation" : true, "allowEdgeOverflow" : false});
        }
        {
            var Q0;
            Q0=makeQuery(id+"F2.opExtrude","SWEPT_EDGE",EDGE,{"disambiguationData":[OSD([sQuery(id+"F0.wireOp",EDGE,"E1.top"),sQuery(id+"F0.wireOp",EDGE,"E1.left")])]});
            fillet(context, id + "F12", {"entities" : qUnion([Q0]), "radius" : 1 * mm, "tangentPropagation" : true, "allowEdgeOverflow" : false});
        }
        {
            var Q0;
            Q0=makeQuery(id+"F9.opExtrude","SWEPT_EDGE",EDGE,{"disambiguationData":[OSD([sQuery(id+"F8.wireOp",EDGE,"E311.top"),sQuery(id+"F8.wireOp",EDGE,"E311.right")])]});
            var Q1;
            Q1=makeQuery(id+"F9.opExtrude","SWEPT_EDGE",EDGE,{"disambiguationData":[OSD([sQuery(id+"F8.wireOp",EDGE,"E311.top"),sQuery(id+"F8.wireOp",EDGE,"E311.left")])]});
            var Q2;
            Q2=makeQuery(id+"F7.opExtrude","SWEPT_EDGE",EDGE,{"disambiguationData":[OSD([sQuery(id+"F5.wireOp",EDGE,"E310.bottom"),sQuery(id+"F5.wireOp",EDGE,"E310.left")])]});
            fillet(context, id + "F13", {"entities" : qUnion([Q0, Q1, Q2]), "radius" : 4 * mm, "tangentPropagation" : true, "allowEdgeOverflow" : false});
        }
        {
            var Q0;
            Q0=makeQuery(id+"F2.opExtrude","CAP_FACE",FACE,{"disambiguationData":[OSD([sQuery(id+"F0.wireOp",EDGE,"E0.bottom"),sQuery(id+"F0.wireOp",EDGE,"E0.top"),sQuery(id+"F0.wireOp",EDGE,"E0.left"),sQuery(id+"F0.wireOp",EDGE,"E1.top"),sQuery(id+"F0.wireOp",EDGE,"E1.left"),sQuery(id+"F0.wireOp",EDGE,"E2")])],"isStart":false});
            cPlane(context, id + "F14", {"entities" : qUnion([Q0]), "cplaneType" : CPlaneType.OFFSET, "offset" : 0 * mm, "width" : 150 * mm, "height" : 150 * mm});
        }
        {
            var Q0;
            Q0=qCreatedBy(id+"F14.planeOp",FACE);
            var sketch = newSketch(context, id + "F15", { "sketchPlane" : qUnion([Q0])});
            skPoint(sketch, "E312", {"position": v(-69, 116.6) * mm});
            skSolve(sketch);
        }
        {
            var Q0;
            Q0=makeQuery(id+"F9.boolean.opBoolean","INTERSECT",EDGE,{"derivedFrom":[makeQuery(id+"F2.opExtrude","CAP_FACE",FACE,{"disambiguationData":[OSD([sQuery(id+"F0.wireOp",EDGE,"E0.top"),sQuery(id+"F0.wireOp",EDGE,"E0.left"),sQuery(id+"F0.wireOp",EDGE,"E1.top"),sQuery(id+"F0.wireOp",EDGE,"E1.left"),sQuery(id+"F0.wireOp",EDGE,"aedadd35-a89c-44a4-b081-527595949099"),sQuery(id+"F0.wireOp",EDGE,"E2")])],"isStart":false}),makeQuery(id+"F9.opExtrude","CAP_FACE",FACE,{"disambiguationData":[OSD([sQuery(id+"F8.wireOp",EDGE,"E311.bottom"),sQuery(id+"F8.wireOp",EDGE,"E311.top"),sQuery(id+"F8.wireOp",EDGE,"E311.left"),sQuery(id+"F8.wireOp",EDGE,"E311.right")])],"isStart":true})]});
            var Q1;
            Q1=makeQuery(id+"F9.boolean.opBoolean","INTERSECT",EDGE,{"derivedFrom":[makeQuery(id+"F2.opExtrude","CAP_FACE",FACE,{"disambiguationData":[OSD([sQuery(id+"F0.wireOp",EDGE,"E0.top"),sQuery(id+"F0.wireOp",EDGE,"E0.left"),sQuery(id+"F0.wireOp",EDGE,"E1.top"),sQuery(id+"F0.wireOp",EDGE,"E1.left"),sQuery(id+"F0.wireOp",EDGE,"aedadd35-a89c-44a4-b081-527595949099"),sQuery(id+"F0.wireOp",EDGE,"E2")])],"isStart":false}),makeQuery(id+"F9.opExtrude","SWEPT_FACE",FACE,{"disambiguationData":[OSD([sQuery(id+"F8.wireOp",EDGE,"E311.right")])]})]});
            var Q2;
            Q2=makeQuery(id+"F7.boolean.opBoolean","INTERSECT",EDGE,{"derivedFrom":[makeQuery(id+"F2.opExtrude","CAP_FACE",FACE,{"disambiguationData":[OSD([sQuery(id+"F0.wireOp",EDGE,"E0.top"),sQuery(id+"F0.wireOp",EDGE,"E0.left"),sQuery(id+"F0.wireOp",EDGE,"E1.top"),sQuery(id+"F0.wireOp",EDGE,"E1.left"),sQuery(id+"F0.wireOp",EDGE,"aedadd35-a89c-44a4-b081-527595949099"),sQuery(id+"F0.wireOp",EDGE,"E2")])],"isStart":false}),makeQuery(id+"F7.opExtrude","SWEPT_FACE",FACE,{"disambiguationData":[OSD([sQuery(id+"F5.wireOp",EDGE,"E310.left")])]})]});
            fillet(context, id + "F16", {"entities" : qUnion([Q0, Q1, Q2]), "radius" : 3 * mm, "tangentPropagation" : true, "allowEdgeOverflow" : false});
        }
        {
            var Q0;
            Q0=makeQuery(id+"F2.opExtrude","SWEPT_EDGE",EDGE,{"disambiguationData":[OSD([sQuery(id+"F0.wireOp",EDGE,"E0.bottom"),sQuery(id+"F0.wireOp",EDGE,"E0.left")])]});
            var Q1;
            Q1=makeQuery(id+"F2.opExtrude","SWEPT_EDGE",EDGE,{"disambiguationData":[OSD([sQuery(id+"F0.wireOp",EDGE,"E0.bottom"),sQuery(id+"F0.wireOp",EDGE,"E1.left")])]});
            fillet(context, id + "F17", {"entities" : qUnion([Q0, Q1]), "radius" : 5 * mm, "tangentPropagation" : true, "allowEdgeOverflow" : false});
        }
        {
            var Q0;
            Q0=sQuery(id+"F15.wireOp",VERTEX,"E312");
            var Q1;
            Q1=makeQuery(id+"F2.opExtrude","SWEPT_BODY",BODY,{"disambiguationData":[OSD([sQuery(id+"F0.wireOp",EDGE,"E0.top"),sQuery(id+"F0.wireOp",EDGE,"E0.left"),sQuery(id+"F0.wireOp",EDGE,"E0.right"),sQuery(id+"F0.wireOp",EDGE,"E1.top"),sQuery(id+"F0.wireOp",EDGE,"E1.left"),sQuery(id+"F0.wireOp",EDGE,"E1.right"),sQuery(id+"F0.wireOp",EDGE,"aedadd35-a89c-44a4-b081-527595949099"),sQuery(id+"F0.wireOp",EDGE,"5d9b1bdb-1e1e-4ad1-b13f-3cf6168354ab0.MirrorCS")])]});
            var Q2;
            Q2=makeQuery(id+"F19.opPattern","COPY",BODY,{"derivedFrom":makeQuery(id+"F2.opExtrude","SWEPT_BODY",BODY,{"disambiguationData":[OSD([sQuery(id+"F0.wireOp",EDGE,"E0.top"),sQuery(id+"F0.wireOp",EDGE,"E0.left"),sQuery(id+"F0.wireOp",EDGE,"E0.right"),sQuery(id+"F0.wireOp",EDGE,"E1.top"),sQuery(id+"F0.wireOp",EDGE,"E1.left"),sQuery(id+"F0.wireOp",EDGE,"E1.right"),sQuery(id+"F0.wireOp",EDGE,"aedadd35-a89c-44a4-b081-527595949099"),sQuery(id+"F0.wireOp",EDGE,"5d9b1bdb-1e1e-4ad1-b13f-3cf6168354ab0.MirrorCS")])]}),"instanceName":"1"});
            hole(context, id + "F18", {"style" : HoleStyle.C_SINK, "endStyle" : HoleEndStyle.THROUGH, "holeDiameter" : 4 * mm, "cSinkDiameter" : 7.25 * mm, "cSinkAngle" : 75 * degree, "majorDiameter" : 5 * mm, "isTappedThrough" : true, "tappedDepth" : 12 * mm, "tapClearance" : 3, "locations" : qUnion([Q0]), "scope" : qUnion([Q1, Q2])});
        }
        {
            var Q0;
            Q0=makeQuery(id+"F2.opExtrude","SWEPT_BODY",BODY,{"disambiguationData":[OSD([sQuery(id+"F0.wireOp",EDGE,"E0.top"),sQuery(id+"F0.wireOp",EDGE,"E0.left"),sQuery(id+"F0.wireOp",EDGE,"E0.right"),sQuery(id+"F0.wireOp",EDGE,"E1.top"),sQuery(id+"F0.wireOp",EDGE,"E1.left"),sQuery(id+"F0.wireOp",EDGE,"E1.right"),sQuery(id+"F0.wireOp",EDGE,"aedadd35-a89c-44a4-b081-527595949099"),sQuery(id+"F0.wireOp",EDGE,"5d9b1bdb-1e1e-4ad1-b13f-3cf6168354ab0.MirrorCS")])]});
            var Q1;
            Q1=qCreatedBy(makeId("Right.planeOp"),FACE);
            mirror(context, id + "F19", {"entities" : qUnion([Q0]), "mirrorPlane" : qUnion([Q1])});
        }
    });
